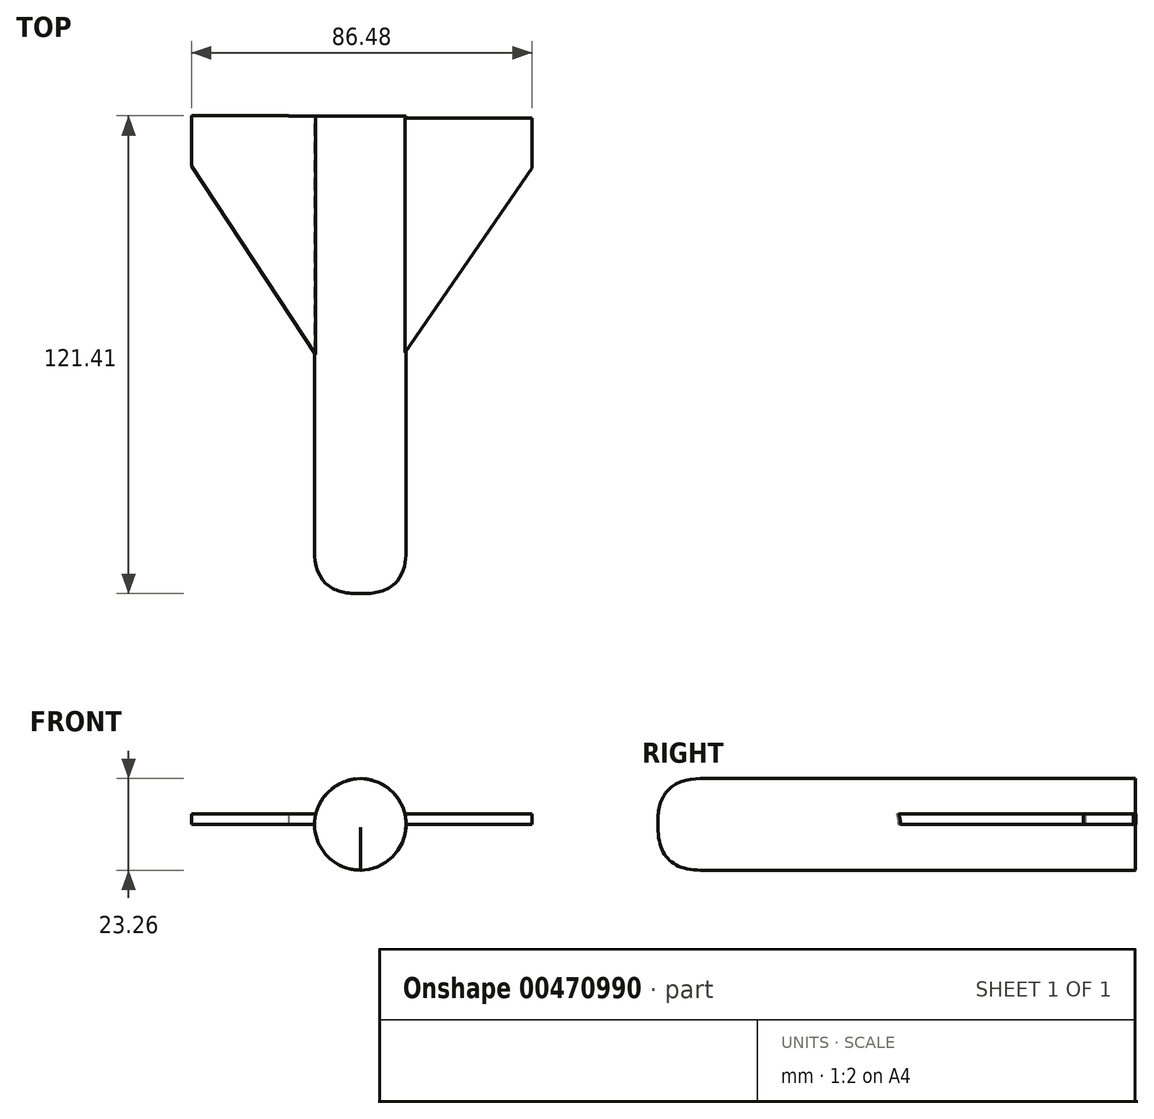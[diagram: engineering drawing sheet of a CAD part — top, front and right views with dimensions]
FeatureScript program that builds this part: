
annotation { "Feature Type Name" : "Feature", "Feature Type Description" : "" }
export const myFeature = defineFeature(function(context is Context, id is Id, definition is map)
    precondition{}
    {
        {
            var Q0;
            Q0=qCreatedBy(makeId("Front.planeOp"),FACE);
            var sketch = newSketch(context, id + "F0", { "sketchPlane" : qUnion([Q0])});
            skCircle(sketch, "E0", {"center": v(0, 0) * mm, "radius": 11.63 * mm});
            skSolve(sketch);
        }
        {
            var Q0;
            Q0=makeQuery(id+"F0.imprint","IMPRINT",FACE,{"disambiguationData":[TD([[makeQuery(id+"F0.imprint","IMPRINT",EDGE,{"derivedFrom":sQuery(id+"F0.wireOp",EDGE,"E0")}),1.0]])]});
            extrude(context, id + "F1", {"entities" : qUnion([Q0]), "depth" : 64 * mm});
        }
        {
            var Q0;
            Q0=makeQuery(id+"F1.opExtrude","CAP_FACE",FACE,{"disambiguationData":[OSD([sQuery(id+"F0.wireOp",EDGE,"E0")])],"isStart":true});
            extrude(context, id + "F2", {"entities" : qUnion([Q0]), "operationType" : NewBodyOperationType.ADD, "depth" : 67.82 * mm});
        }
        {
            var Q0;
            {var subQ0=sQuery(id+"F0.wireOp",EDGE,"E0");Q0=makeQuery(id+"F2.boolean.opBoolean","MERGE",FACE,{"derivedFrom":[makeQuery(id+"F1.opExtrude","SWEPT_FACE",FACE,{"disambiguationData":[OSD([subQ0])]}),makeQuery(id+"F2.opExtrude","SWEPT_FACE",FACE,{"disambiguationData":[OSD([subQ0])]})]});}
            var Q1;
            Q1=makeQuery(id+"F2.opExtrude","CAP_EDGE",EDGE,{"disambiguationData":[OSD([sQuery(id+"F0.wireOp",EDGE,"E0")])],"isStart":false});
            var Q2;
            Q2=makeQuery(id+"F2.opExtrude","CAP_FACE",FACE,{"disambiguationData":[OSD([sQuery(id+"F0.wireOp",EDGE,"E0")])],"isStart":false});
            fillet(context, id + "F3", {"entities" : qUnion([Q0, Q1, Q2]), "radius" : 10.86 * mm, "tangentPropagation" : true, "rho" : 0.5, "crossSection" : FilletCrossSection.CONIC, "allowEdgeOverflow" : false});
        }
        {
            var Q0;
            Q0=qCreatedBy(makeId("Top.planeOp"),FACE);
            var sketch = newSketch(context, id + "F4", { "sketchPlane" : qUnion([Q0])});
            skLineSegment(sketch, "E1", {"start": v(10.97, 56.82) * mm, "end": v(43.61, 56.82) * mm});
            skLineSegment(sketch, "E2", {"start": v(43.61, 56.82) * mm, "end": v(43.61, 44.06) * mm});
            skLineSegment(sketch, "E3", {"start": v(43.61, 44.06) * mm, "end": v(10.52, -3.98) * mm});
            skLineSegment(sketch, "E4", {"start": v(10.52, -3.98) * mm, "end": v(10.97, 56.82) * mm});
            skLineSegment(sketch, "E5", {"start": v(-10.22, 57.4) * mm, "end": v(-42.87, 57.4) * mm});
            skLineSegment(sketch, "E6", {"start": v(-42.87, 57.4) * mm, "end": v(-42.87, 44.65) * mm});
            skLineSegment(sketch, "E7", {"start": v(-42.87, 44.65) * mm, "end": v(-10.82, -4.1) * mm});
            skLineSegment(sketch, "E8", {"start": v(-10.82, -4.1) * mm, "end": v(-10.22, 57.4) * mm});
            skSolve(sketch);
        }
        {
            var Q0;
            Q0 = qSketchRegion(id + "F4", true);
            extrude(context, id + "F5", {"entities" : qUnion([Q0]), "operationType" : NewBodyOperationType.ADD, "depth" : 2.6 * mm});
        }
        {
            var Q0;
            Q0=makeQuery(id+"F1.opExtrude","SWEPT_BODY",BODY,{"disambiguationData":[OSD([sQuery(id+"F0.wireOp",EDGE,"E0")])]});
            var Q1;
            Q1=qCreatedBy(makeId("Origin.pointOp"),VERTEX);
            var Q2;
            {var subQ0=sQuery(id+"F0.wireOp",EDGE,"E0");Q2=makeQuery(id+"F5.boolean.opBoolean","INTERSECT",EDGE,{"derivedFrom":[makeQuery(id+"F2.boolean.opBoolean","MERGE",FACE,{"derivedFrom":[makeQuery(id+"F1.opExtrude","SWEPT_FACE",FACE,{"disambiguationData":[OSD([subQ0])]}),makeQuery(id+"F2.opExtrude","SWEPT_FACE",FACE,{"disambiguationData":[OSD([subQ0])]})]}),makeQuery(id+"F5.opExtrude","CAP_FACE",FACE,{"disambiguationData":[OSD([sQuery(id+"F4.wireOp",EDGE,"E1"),sQuery(id+"F4.wireOp",EDGE,"E2"),sQuery(id+"F4.wireOp",EDGE,"E3"),sQuery(id+"F4.wireOp",EDGE,"E4")])],"isStart":true})]});}
            transform(context, id + "F6", {"entities" : qUnion([Q0]), "transformType" : TransformType.TRANSLATION_DISTANCE, "transformDirection" : qUnion([Q1, Q2]), "distance" : 57.3 * mm, "oppositeDirection" : true, "makeCopy" : false});
        }
        {
            var Q0;
            Q0=qCreatedBy(makeId("Front.planeOp"),FACE);
            var sketch = newSketch(context, id + "F7", { "sketchPlane" : qUnion([Q0])});
            skLineSegment(sketch, "E9.bottom", {"start": v(-18.23, 23.49) * mm, "end": v(18.23, 23.49) * mm});
            skLineSegment(sketch, "E9.top", {"start": v(-18.23, -23.49) * mm, "end": v(18.23, -23.49) * mm});
            skLineSegment(sketch, "E9.left", {"start": v(-18.23, 23.49) * mm, "end": v(-18.23, -23.49) * mm});
            skLineSegment(sketch, "E9.right", {"start": v(18.23, 23.49) * mm, "end": v(18.23, -23.49) * mm});
            skPoint(sketch, "E9.middle", {"position": v(0, 0) * mm});
            skSolve(sketch);
        }
        {
            var Q0;
            Q0 = qSketchRegion(id + "F7", true);
            extrude(context, id + "F8", {"entities" : qUnion([Q0]), "operationType" : NewBodyOperationType.REMOVE, "oppositeDirection" : true, "depth" : 32 * mm});
        }
    });
